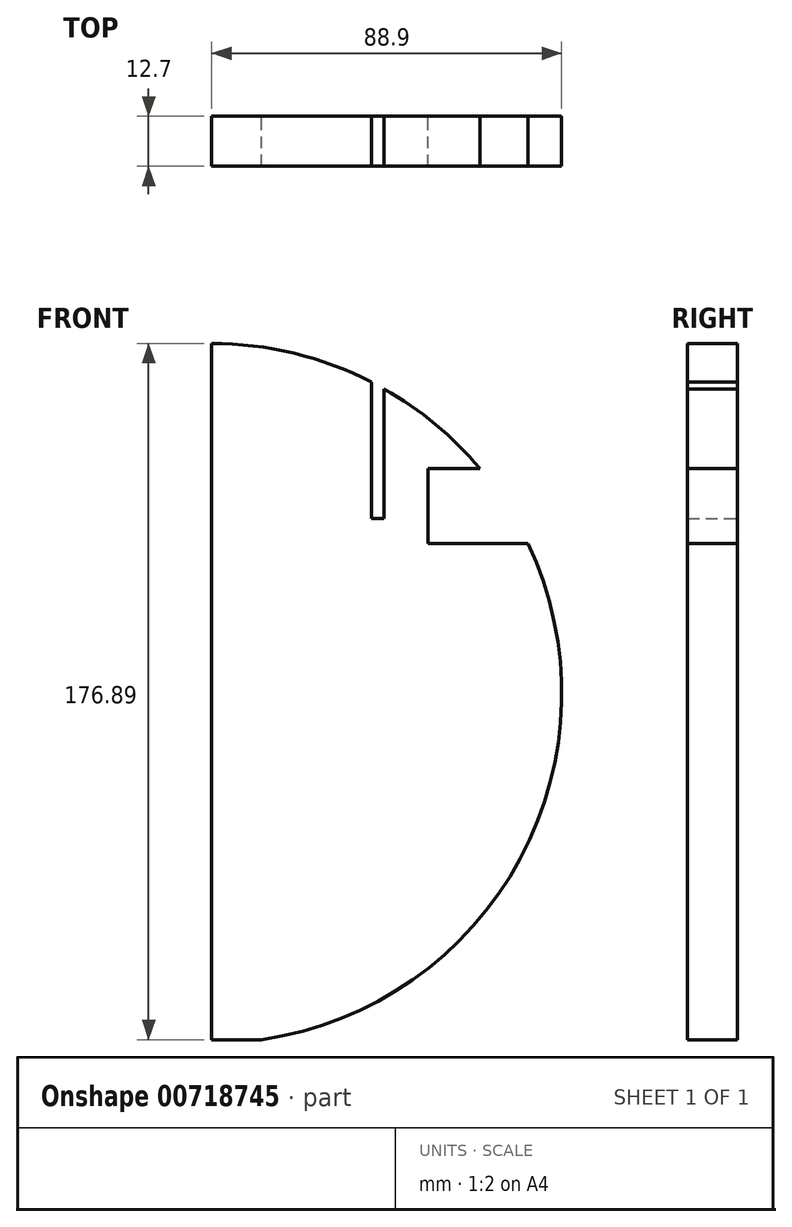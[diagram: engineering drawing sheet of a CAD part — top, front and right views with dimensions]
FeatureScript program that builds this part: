
annotation { "Feature Type Name" : "Feature", "Feature Type Description" : "" }
export const myFeature = defineFeature(function(context is Context, id is Id, definition is map)
    precondition{}
    {
        {
            var Q0;
            Q0=qCreatedBy(makeId("Front.planeOp"),FACE);
            var sketch = newSketch(context, id + "F0", { "sketchPlane" : qUnion([Q0])});
            skLineSegment(sketch, "E0", {"start": v(0, 88.9) * mm, "end": v(0, -88.9) * mm});
            skArc(sketch, "E1", {"start": v(0, -88.9) * mm, "mid": v(88.9, 0) * mm, "end": v(0, 88.9) * mm});
            skLineSegment(sketch, "E2", {"start": v(68.1, 57.15) * mm, "end": v(54.92, 57.15) * mm});
            skLineSegment(sketch, "E3", {"start": v(54.92, 57.15) * mm, "end": v(54.92, 38.1) * mm});
            skLineSegment(sketch, "E4", {"start": v(54.92, 38.1) * mm, "end": v(80.32, 38.1) * mm});
            skLineSegment(sketch, "E5", {"start": v(42.22, 78.23) * mm, "end": v(42.22, 27.49) * mm, "construction": true});
            skLineSegment(sketch, "E6", {"start": v(40.63, 79.07) * mm, "end": v(40.63, 44.45) * mm});
            skLineSegment(sketch, "E7", {"start": v(40.63, 44.45) * mm, "end": v(43.8, 44.45) * mm});
            skLineSegment(sketch, "E8", {"start": v(43.8, 44.45) * mm, "end": v(43.8, 77.36) * mm});
            skLineSegment(sketch, "E9", {"start": v(0, -87.99) * mm, "end": v(12.7, -87.99) * mm});
            skSolve(sketch);
        }
        {
            var Q0;
            {var subQ2=sQuery(id+"F0.wireOp",EDGE,"E2");Q0=makeQuery(id+"F0.imprint","IMPRINT",FACE,{"disambiguationData":[TD([[makeQuery(id+"F0.imprint","IMPRINT",EDGE,{"derivedFrom":subQ2}),-1.0]])]});}
            extrude(context, id + "F1", {"entities" : qUnion([Q0]), "depth" : 12.7 * mm, "offsetDistance" : 25.4 * mm});
        }
    });
